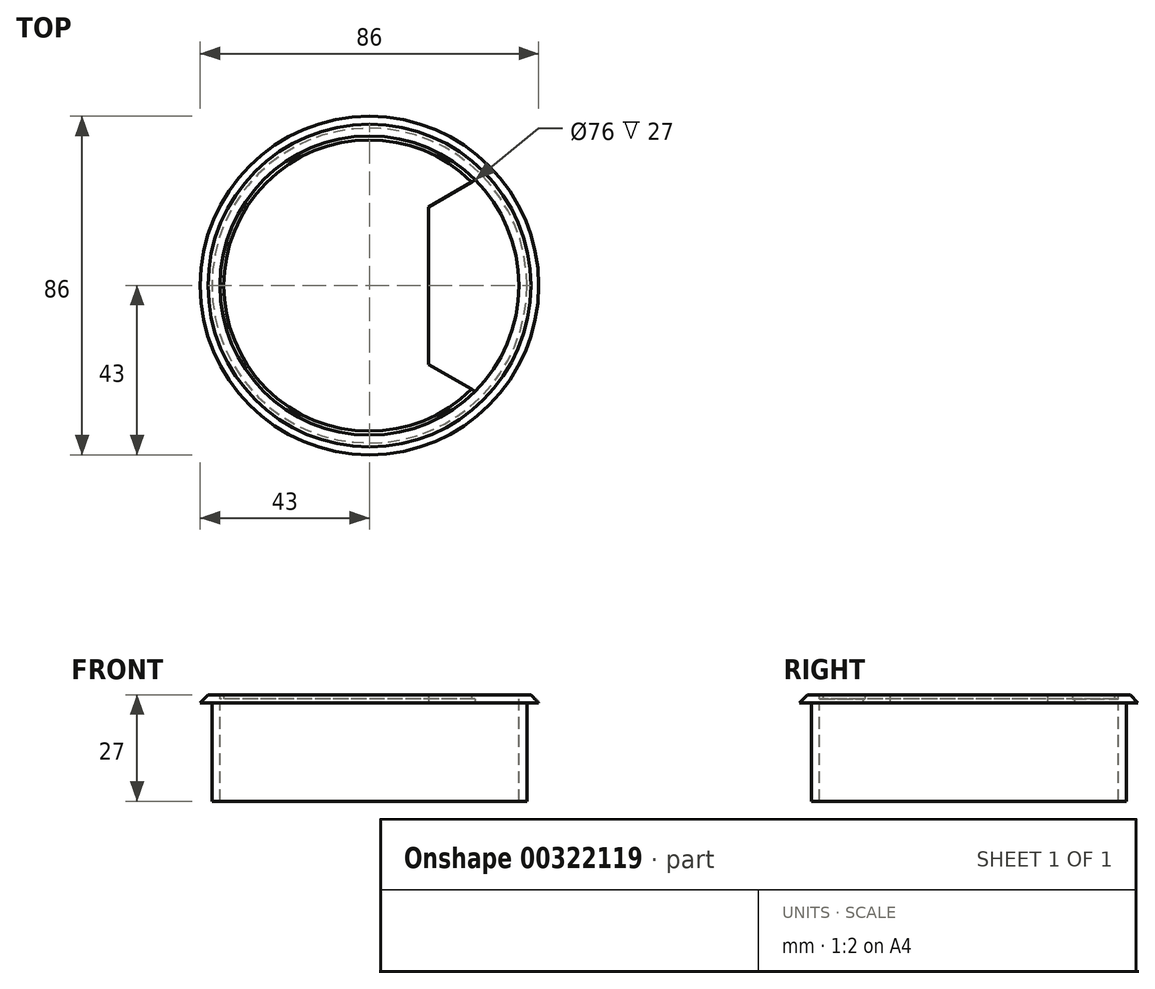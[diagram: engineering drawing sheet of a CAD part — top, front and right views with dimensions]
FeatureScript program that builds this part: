
annotation { "Feature Type Name" : "Feature", "Feature Type Description" : "" }
export const myFeature = defineFeature(function(context is Context, id is Id, definition is map)
    precondition{}
    {
        {
            var Q0;
            Q0=qCreatedBy(makeId("Front.planeOp"),FACE);
            var sketch = newSketch(context, id + "F0", { "sketchPlane" : qUnion([Q0])});
            skLineSegment(sketch, "E0", {"start": v(0, 0) * mm, "end": v(0, -87.77) * mm, "construction": true});
            skLineSegment(sketch, "E1", {"start": v(-38, 2) * mm, "end": v(-38, -25) * mm});
            skLineSegment(sketch, "E2", {"start": v(-38, -25) * mm, "end": v(-40, -25) * mm});
            skLineSegment(sketch, "E3", {"start": v(-40, -25) * mm, "end": v(-40, 0) * mm});
            skLineSegment(sketch, "E4", {"start": v(-40, 0) * mm, "end": v(-43, 0) * mm});
            skLineSegment(sketch, "E5", {"start": v(-43, 0) * mm, "end": v(-41, 2) * mm});
            skLineSegment(sketch, "E6", {"start": v(-41, 2) * mm, "end": v(-38, 2) * mm});
            skSolve(sketch);
        }
        {
            var Q0;
            Q0=makeQuery(id+"F0.imprint","IMPRINT",FACE,{"disambiguationData":[TD([[makeQuery(id+"F0.imprint","IMPRINT",EDGE,{"derivedFrom":sQuery(id+"F0.wireOp",EDGE,"E1")}),-1.0]])]});
            var Q1;
            Q1=sQuery(id+"F0.wireOp",EDGE,"E0");
            revolve(context, id + "F1", {"entities" : qUnion([Q0]), "axis" : qUnion([Q1]), "revolveType" : RevolveType.FULL});
        }
        {
            var Q0;
            Q0=qCreatedBy(makeId("Top.planeOp"),FACE);
            var sketch = newSketch(context, id + "F2", { "sketchPlane" : qUnion([Q0])});
            skArc(sketch, "E7.0", {"start": v(26.88, 26.86) * mm, "mid": v(-38, 0) * mm, "end": v(26.88, -26.86) * mm});
            skLineSegment(sketch, "E8", {"start": v(26.88, 26.86) * mm, "end": v(15, 20) * mm});
            skLineSegment(sketch, "E9", {"start": v(15, 20) * mm, "end": v(15, -20) * mm});
            skLineSegment(sketch, "E10", {"start": v(15, -20) * mm, "end": v(26.88, -26.86) * mm});
            skLineSegment(sketch, "E11", {"start": v(26.88, -26.86) * mm, "end": v(26.88, 26.86) * mm, "construction": true});
            skLineSegment(sketch, "E12", {"start": v(-38, 0) * mm, "end": v(38, 0) * mm, "construction": true});
            skSolve(sketch);
        }
        {
            var Q0;
            Q0=makeQuery(id+"F2.imprint","IMPRINT",FACE,{"disambiguationData":[TD([[makeQuery(id+"F2.imprint","IMPRINT",EDGE,{"derivedFrom":sQuery(id+"F2.wireOp",EDGE,"E7.0")}),1.0]])]});
            extrude(context, id + "F3", {"entities" : qUnion([Q0]), "operationType" : NewBodyOperationType.ADD, "depth" : 1 * mm});
        }
        {
            var Q0;
            Q0=makeQuery(id+"F3.opExtrude","CAP_FACE",FACE,{"disambiguationData":[OSD([sQuery(id+"F2.wireOp",EDGE,"E7.0"),sQuery(id+"F2.wireOp",EDGE,"E8"),sQuery(id+"F2.wireOp",EDGE,"E9"),sQuery(id+"F2.wireOp",EDGE,"E10")])],"isStart":false});
            var sketch = newSketch(context, id + "F4", { "sketchPlane" : qUnion([Q0])});
            skArc(sketch, "E13.0", {"start": v(26.88, 26.86) * mm, "mid": v(-38, 0) * mm, "end": v(26.88, -26.86) * mm, "construction": true});
            skArc(sketch, "E14.0", {"start": v(25.98, 26.34) * mm, "mid": v(-37, 0) * mm, "end": v(25.98, -26.34) * mm});
            skLineSegment(sketch, "E15.0", {"start": v(25.98, 26.34) * mm, "end": v(15, 20) * mm});
            skLineSegment(sketch, "E16.0", {"start": v(15, 20) * mm, "end": v(15, -20) * mm});
            skLineSegment(sketch, "E17.0", {"start": v(15, -20) * mm, "end": v(25.98, -26.34) * mm});
            skSolve(sketch);
        }
        {
            var Q0;
            Q0=makeQuery(id+"F4.imprint","IMPRINT",FACE,{"disambiguationData":[TD([[makeQuery(id+"F4.imprint","IMPRINT",EDGE,{"derivedFrom":sQuery(id+"F4.wireOp",EDGE,"E14.0")}),1.0]])]});
            var Q1;
            Q1=makeQuery(id+"F1.opRevolve","SWEPT_FACE",FACE,{"disambiguationData":[OSD([sQuery(id+"F0.wireOp",EDGE,"E6")])]});
            extrude(context, id + "F5", {"entities" : qUnion([Q0]), "operationType" : NewBodyOperationType.ADD, "endBound" : BoundingType.UP_TO_SURFACE, "endBoundEntityFace" : qUnion([Q1]), "depth" : 25 * mm});
        }
    });
